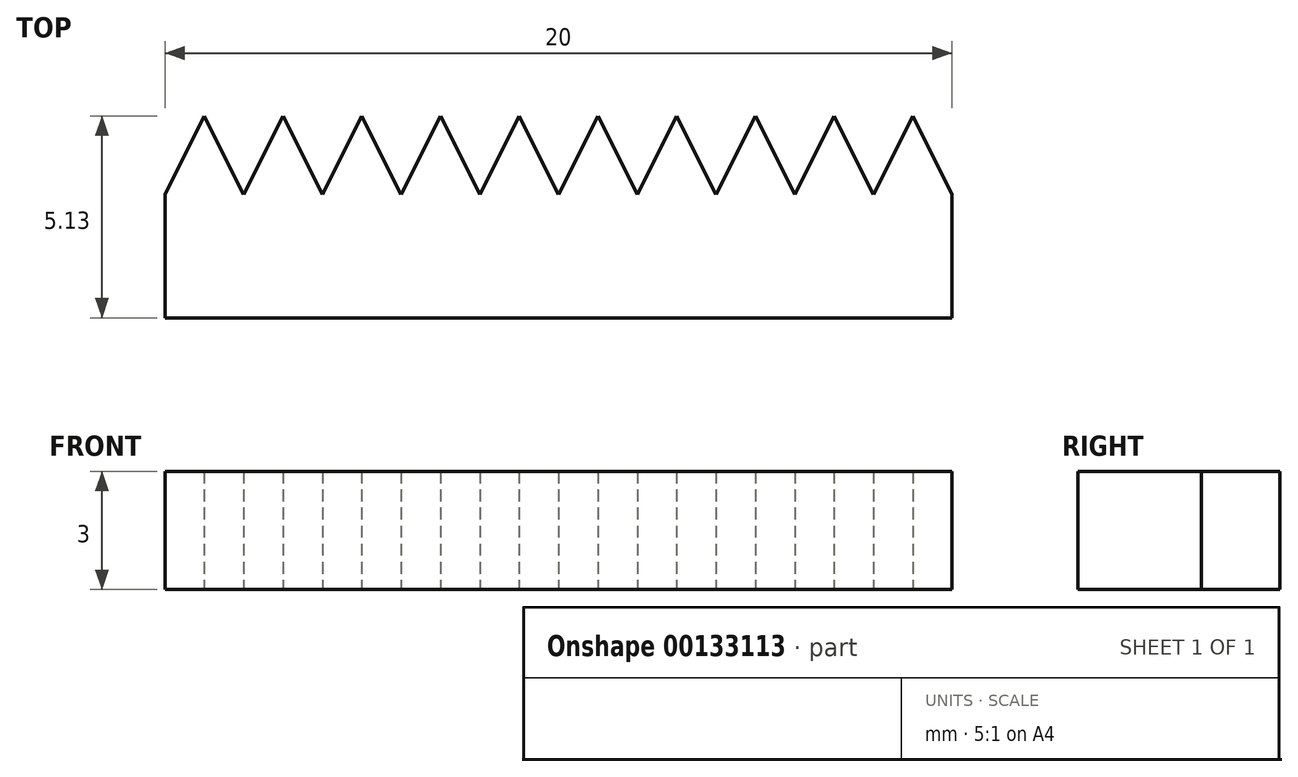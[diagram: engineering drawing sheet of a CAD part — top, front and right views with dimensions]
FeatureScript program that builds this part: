
annotation { "Feature Type Name" : "Feature", "Feature Type Description" : "" }
export const myFeature = defineFeature(function(context is Context, id is Id, definition is map)
    precondition{}
    {
        {
            var Q0;
            Q0=qCreatedBy(makeId("Top.planeOp"),FACE);
            var sketch = newSketch(context, id + "F0", { "sketchPlane" : qUnion([Q0])});
            skLineSegment(sketch, "E0.bottom", {"start": v(0, 0) * mm, "end": v(20, 0) * mm});
            skLineSegment(sketch, "E0.top", {"start": v(0, -3.13) * mm, "end": v(20, -3.13) * mm});
            skLineSegment(sketch, "E0.left", {"start": v(0, 0) * mm, "end": v(0, -3.13) * mm});
            skLineSegment(sketch, "E0.right", {"start": v(20, 0) * mm, "end": v(20, -3.13) * mm});
            skLineSegment(sketch, "E1", {"start": v(0, 0) * mm, "end": v(1, 2) * mm});
            skLineSegment(sketch, "E2", {"start": v(1, 2) * mm, "end": v(2, 0) * mm});
            skPoint(sketch, "E3", {"position": v(2, 0) * mm});
            skLineSegment(sketch, "E4", {"start": v(0, 0) * mm, "end": v(2, 0) * mm, "construction": true});
            skLineSegment(sketch, "E5.1.0.0", {"start": v(3, 2) * mm, "end": v(4, 0) * mm});
            skLineSegment(sketch, "E5.1.0.1", {"start": v(2, 0) * mm, "end": v(3, 2) * mm});
            skLineSegment(sketch, "E5.2.0.0", {"start": v(5, 2) * mm, "end": v(6, 0) * mm});
            skLineSegment(sketch, "E5.2.0.1", {"start": v(4, 0) * mm, "end": v(5, 2) * mm});
            skLineSegment(sketch, "E5.3.0.0", {"start": v(7, 2) * mm, "end": v(8, 0) * mm});
            skLineSegment(sketch, "E5.3.0.1", {"start": v(6, 0) * mm, "end": v(7, 2) * mm});
            skLineSegment(sketch, "E5.4.0.0", {"start": v(9, 2) * mm, "end": v(10, 0) * mm});
            skLineSegment(sketch, "E5.4.0.1", {"start": v(8, 0) * mm, "end": v(9, 2) * mm});
            skLineSegment(sketch, "E5.5.0.0", {"start": v(11, 2) * mm, "end": v(12, 0) * mm});
            skLineSegment(sketch, "E5.5.0.1", {"start": v(10, 0) * mm, "end": v(11, 2) * mm});
            skLineSegment(sketch, "E5.6.0.0", {"start": v(13, 2) * mm, "end": v(14, 0) * mm});
            skLineSegment(sketch, "E5.6.0.1", {"start": v(12, 0) * mm, "end": v(13, 2) * mm});
            skLineSegment(sketch, "E5.7.0.0", {"start": v(15, 2) * mm, "end": v(16, 0) * mm});
            skLineSegment(sketch, "E5.7.0.1", {"start": v(14, 0) * mm, "end": v(15, 2) * mm});
            skLineSegment(sketch, "E5.8.0.0", {"start": v(17, 2) * mm, "end": v(18, 0) * mm});
            skLineSegment(sketch, "E5.8.0.1", {"start": v(16, 0) * mm, "end": v(17, 2) * mm});
            skLineSegment(sketch, "E5.9.0.0", {"start": v(19, 2) * mm, "end": v(20, 0) * mm});
            skLineSegment(sketch, "E5.9.0.1", {"start": v(18, 0) * mm, "end": v(19, 2) * mm});
            skLineSegment(sketch, "E5.direction1", {"start": v(2, 0) * mm, "end": v(4, 0) * mm, "construction": true});
            skSolve(sketch);
        }
        {
            var Q0;
            Q0 = qSketchRegion(id + "F0", true);
            extrude(context, id + "F1", {"entities" : qUnion([Q0]), "depth" : 3 * mm});
        }
    });
